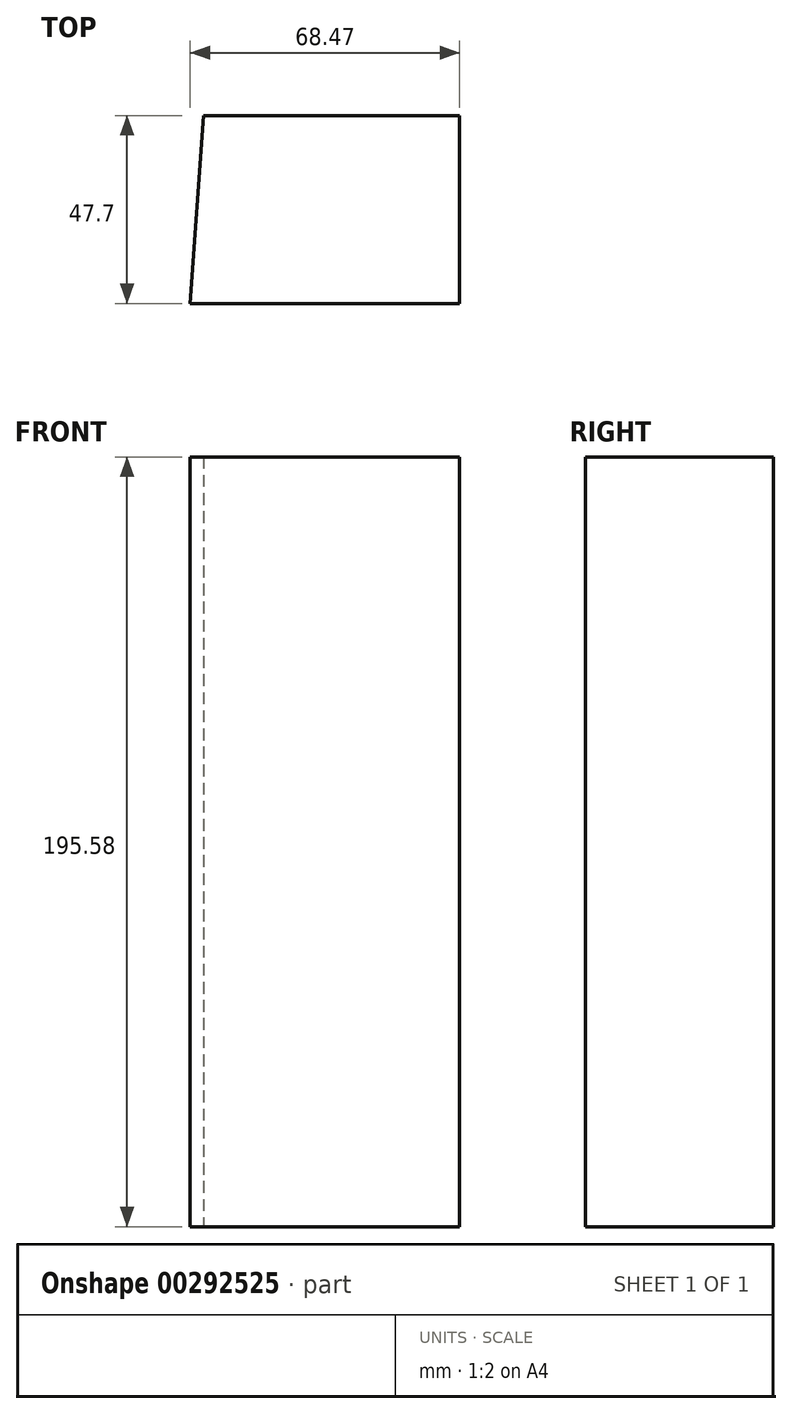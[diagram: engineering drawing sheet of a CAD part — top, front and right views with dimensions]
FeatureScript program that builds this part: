
annotation { "Feature Type Name" : "Feature", "Feature Type Description" : "" }
export const myFeature = defineFeature(function(context is Context, id is Id, definition is map)
    precondition{}
    {
        {
            var Q0;
            Q0=qCreatedBy(makeId("Top.planeOp"),FACE);
            var sketch = newSketch(context, id + "F0", { "sketchPlane" : qUnion([Q0])});
            skLineSegment(sketch, "E0", {"start": v(0, 0) * mm, "end": v(68.47, 0) * mm});
            skLineSegment(sketch, "E1", {"start": v(68.47, 0) * mm, "end": v(68.47, 47.7) * mm});
            skLineSegment(sketch, "E2", {"start": v(68.47, 47.7) * mm, "end": v(3.45, 47.7) * mm});
            skLineSegment(sketch, "E3", {"start": v(3.45, 47.7) * mm, "end": v(0, 0) * mm});
            skSolve(sketch);
        }
        {
            var Q0;
            Q0=makeQuery(id+"F0.imprint","IMPRINT",FACE,{"disambiguationData":[TD([[makeQuery(id+"F0.imprint","IMPRINT",EDGE,{"derivedFrom":sQuery(id+"F0.wireOp",EDGE,"E0")}),1.0]])]});
            extrude(context, id + "F1", {"entities" : qUnion([Q0]), "depth" : 195.58 * mm});
        }
    });
